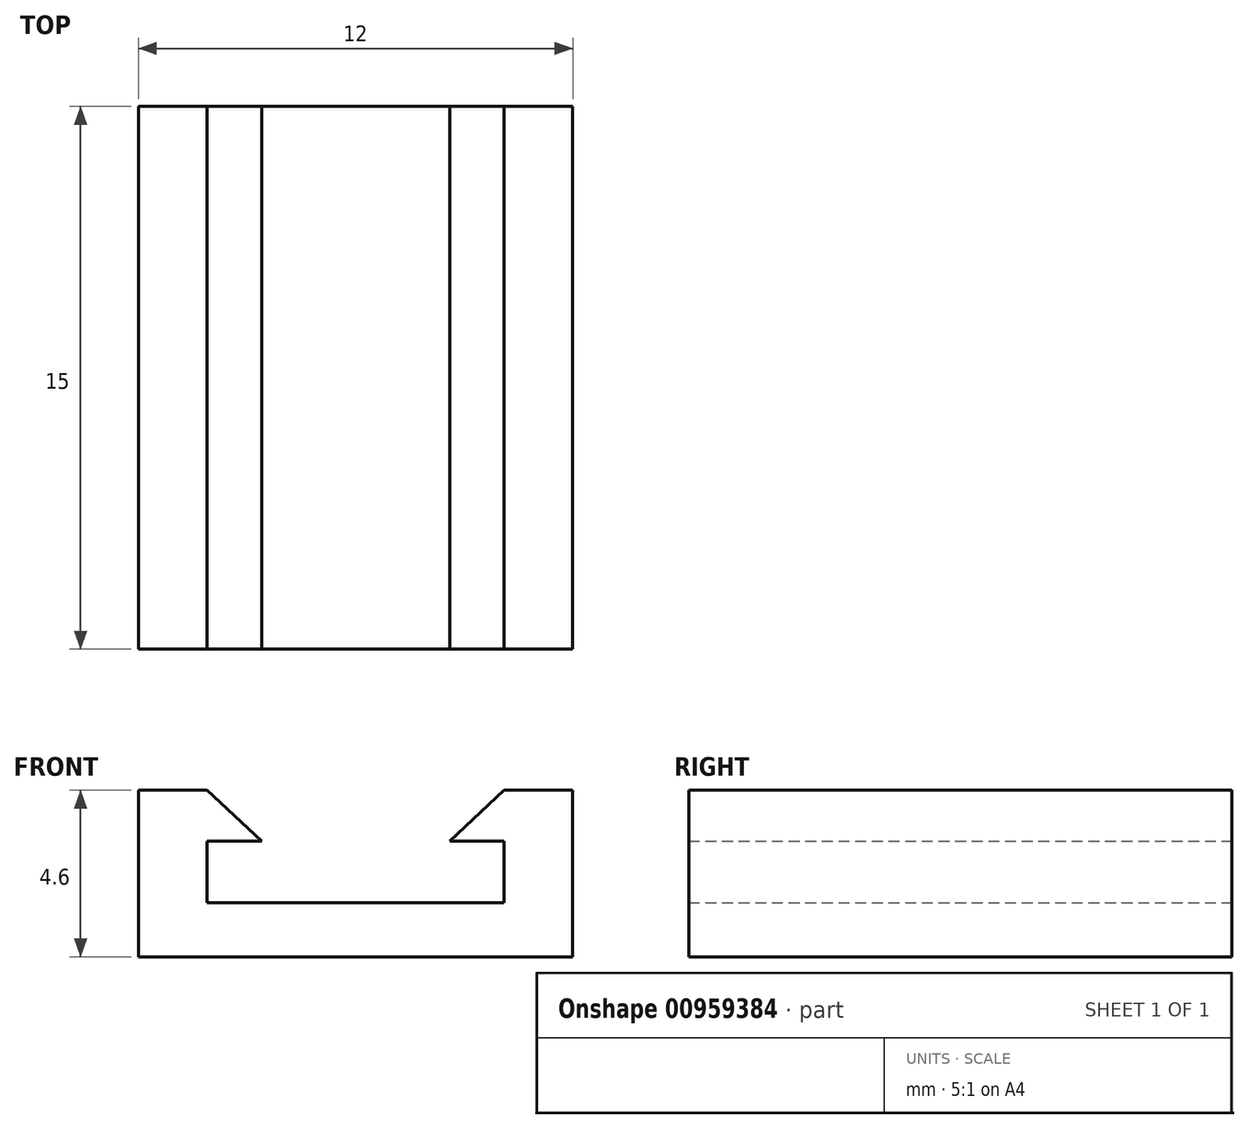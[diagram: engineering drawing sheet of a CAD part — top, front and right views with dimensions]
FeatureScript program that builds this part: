
annotation { "Feature Type Name" : "Feature", "Feature Type Description" : "" }
export const myFeature = defineFeature(function(context is Context, id is Id, definition is map)
    precondition{}
    {
        {
            var Q0;
            Q0=qCreatedBy(makeId("Front.planeOp"),FACE);
            var sketch = newSketch(context, id + "F0", { "sketchPlane" : qUnion([Q0])});
            skLineSegment(sketch, "E0", {"start": v(-4.1, 3.24) * mm, "end": v(-6, 3.24) * mm});
            skLineSegment(sketch, "E1", {"start": v(-6, 3.24) * mm, "end": v(-6, -1.36) * mm});
            skLineSegment(sketch, "E2", {"start": v(-6, -1.36) * mm, "end": v(0, -1.36) * mm});
            skLineSegment(sketch, "E3", {"start": v(0, -1.36) * mm, "end": v(0, 0.14) * mm, "construction": true});
            skLineSegment(sketch, "E4", {"start": v(0, 0.14) * mm, "end": v(-4.1, 0.14) * mm});
            skLineSegment(sketch, "E5", {"start": v(-4.1, 0.14) * mm, "end": v(-4.1, 1.84) * mm});
            skLineSegment(sketch, "E6", {"start": v(-4.1, 1.84) * mm, "end": v(-2.6, 1.84) * mm});
            skLineSegment(sketch, "E7", {"start": v(-2.6, 1.84) * mm, "end": v(-4.1, 3.24) * mm});
            skLineSegment(sketch, "E8.MirrorCS", {"start": v(0, 0.14) * mm, "end": v(4.1, 0.14) * mm});
            skLineSegment(sketch, "E9.MirrorCS", {"start": v(4.1, 1.84) * mm, "end": v(2.6, 1.84) * mm});
            skLineSegment(sketch, "E10.MirrorCS", {"start": v(4.1, 0.14) * mm, "end": v(4.1, 1.84) * mm});
            skLineSegment(sketch, "E11.MirrorCS", {"start": v(2.6, 1.84) * mm, "end": v(4.1, 3.24) * mm});
            skLineSegment(sketch, "E12.MirrorCS", {"start": v(4.1, 3.24) * mm, "end": v(6, 3.24) * mm});
            skLineSegment(sketch, "E13.MirrorCS", {"start": v(6, 3.24) * mm, "end": v(6, -1.36) * mm});
            skLineSegment(sketch, "E14.MirrorCS", {"start": v(6, -1.36) * mm, "end": v(0, -1.36) * mm});
            skSolve(sketch);
        }
        {
            var Q0;
            Q0=makeQuery(id+"F0.imprint","IMPRINT",FACE,{"disambiguationData":[TD([[makeQuery(id+"F0.imprint","IMPRINT",EDGE,{"derivedFrom":sQuery(id+"F0.wireOp",EDGE,"E0")}),1.0]])]});
            extrude(context, id + "F1", {"entities" : qUnion([Q0]), "depth" : 15 * mm, "offsetDistance" : 25 * mm});
        }
    });
